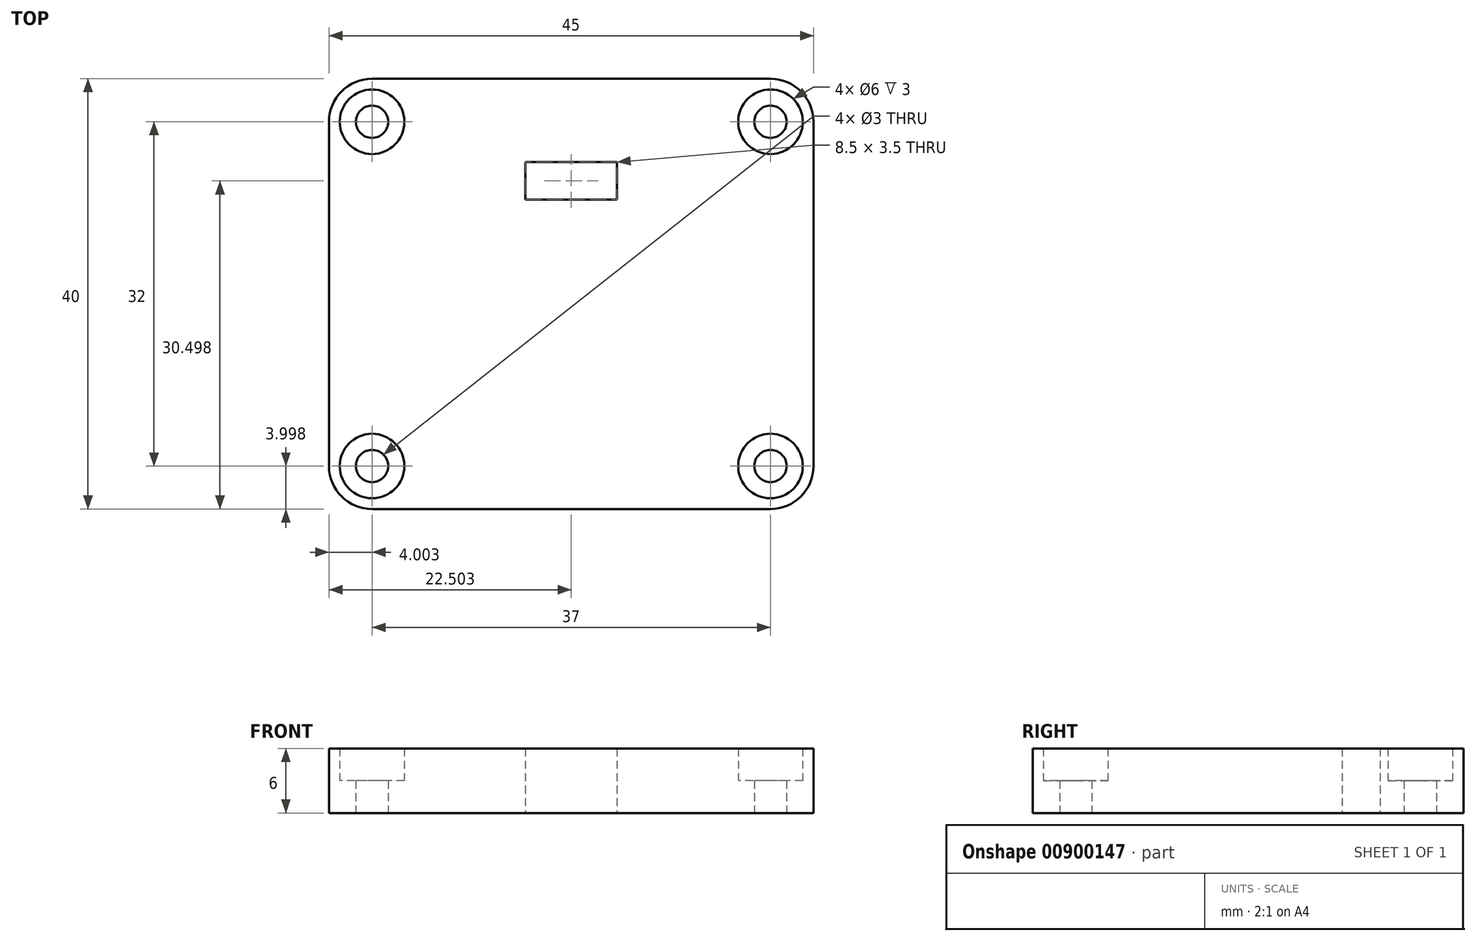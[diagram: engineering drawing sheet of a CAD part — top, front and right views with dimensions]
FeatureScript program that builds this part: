
annotation { "Feature Type Name" : "Feature", "Feature Type Description" : "" }
export const myFeature = defineFeature(function(context is Context, id is Id, definition is map)
    precondition{}
    {
        {
            var Q0;
            Q0=qCreatedBy(makeId("Top.planeOp"),FACE);
            var sketch = newSketch(context, id + "F0", { "sketchPlane" : qUnion([Q0])});
            skLineSegment(sketch, "E0", {"start": v(-24.6, 14.45) * mm, "end": v(-24.6, -17.55) * mm});
            skLineSegment(sketch, "E1", {"start": v(-20.6, -21.55) * mm, "end": v(16.4, -21.55) * mm});
            skLineSegment(sketch, "E2", {"start": v(20.4, -17.55) * mm, "end": v(20.4, 14.45) * mm});
            skLineSegment(sketch, "E3", {"start": v(16.4, 18.45) * mm, "end": v(-20.6, 18.45) * mm});
            skPoint(sketch, "E4.visualSharp", {"position": v(-24.6, 18.45) * mm});
            skArc(sketch, "E4.filletArc", {"start": v(-20.6, 18.45) * mm, "mid": v(-23.44, 17.28) * mm, "end": v(-24.6, 14.45) * mm});
            skPoint(sketch, "E5.visualSharp", {"position": v(20.4, 18.45) * mm});
            skArc(sketch, "E5.filletArc", {"start": v(20.4, 14.45) * mm, "mid": v(19.22, 17.28) * mm, "end": v(16.4, 18.45) * mm});
            skPoint(sketch, "E6.visualSharp", {"position": v(20.4, -21.55) * mm});
            skArc(sketch, "E6.filletArc", {"start": v(16.4, -21.55) * mm, "mid": v(19.22, -20.38) * mm, "end": v(20.4, -17.55) * mm});
            skPoint(sketch, "E7.visualSharp", {"position": v(-24.6, -21.55) * mm});
            skArc(sketch, "E7.filletArc", {"start": v(-24.6, -17.55) * mm, "mid": v(-23.44, -20.38) * mm, "end": v(-20.6, -21.55) * mm});
            skCircle(sketch, "E8", {"center": v(-20.6, 14.45) * mm, "radius": 1.5 * mm});
            skCircle(sketch, "E9", {"center": v(16.4, 14.45) * mm, "radius": 1.5 * mm});
            skCircle(sketch, "E10", {"center": v(16.4, -17.55) * mm, "radius": 1.5 * mm});
            skCircle(sketch, "E11", {"center": v(-20.6, -17.55) * mm, "radius": 1.5 * mm});
            skLineSegment(sketch, "E12", {"start": v(-14.36, 10.7) * mm, "end": v(-14.36, -13.8) * mm});
            skLineSegment(sketch, "E13", {"start": v(-14.36, -13.8) * mm, "end": v(10.14, -13.8) * mm});
            skLineSegment(sketch, "E14", {"start": v(10.14, -13.8) * mm, "end": v(10.14, 10.7) * mm});
            skLineSegment(sketch, "E15", {"start": v(10.14, 10.7) * mm, "end": v(-14.36, 10.7) * mm});
            skLineSegment(sketch, "E16", {"start": v(-6.36, 7.2) * mm, "end": v(2.14, 7.2) * mm});
            skLineSegment(sketch, "E17", {"start": v(2.14, 7.2) * mm, "end": v(2.14, 10.7) * mm});
            skLineSegment(sketch, "E18", {"start": v(-6.36, 7.2) * mm, "end": v(-6.36, 10.7) * mm});
            skLineSegment(sketch, "E19", {"start": v(-2.1, 18.45) * mm, "end": v(-2.1, -21.55) * mm, "construction": true});
            skLineSegment(sketch, "E20", {"start": v(-24.6, -1.55) * mm, "end": v(20.4, -1.55) * mm, "construction": true});
            skCircle(sketch, "E21", {"center": v(-20.6, 14.45) * mm, "radius": 3 * mm});
            skCircle(sketch, "E22.MirrorC", {"center": v(16.4, 14.45) * mm, "radius": 3 * mm});
            skCircle(sketch, "E23.MirrorC", {"center": v(16.4, -17.55) * mm, "radius": 3 * mm});
            skCircle(sketch, "E24.MirrorC", {"center": v(-20.6, -17.55) * mm, "radius": 3 * mm});
            skSolve(sketch);
        }
        {
            var Q0;
            Q0 = qSketchRegion(id + "F0", true);
            var Q1;
            {var subQ3=sQuery(id+"F0.wireOp",EDGE,"E12");Q1=makeQuery(id+"F0.imprint","IMPRINT",FACE,{"disambiguationData":[TD([[makeQuery(id+"F0.imprint","IMPRINT",EDGE,{"derivedFrom":subQ3}),1.0]])]});}
            extrude(context, id + "F1", {"entities" : qUnion([Q0, Q1]), "depth" : 6 * mm, "offsetDistance" : 25 * mm});
        }
        {
            var Q0;
            Q0=makeQuery(id+"F0.imprint","IMPRINT",FACE,{"disambiguationData":[TD([[makeQuery(id+"F0.imprint","IMPRINT",EDGE,{"derivedFrom":sQuery(id+"F0.wireOp",EDGE,"E8")}),-1.0]])]});
            var Q1;
            Q1=makeQuery(id+"F0.imprint","IMPRINT",FACE,{"disambiguationData":[TD([[makeQuery(id+"F0.imprint","IMPRINT",EDGE,{"derivedFrom":sQuery(id+"F0.wireOp",EDGE,"E9")}),-1.0]])]});
            var Q2;
            Q2=makeQuery(id+"F0.imprint","IMPRINT",FACE,{"disambiguationData":[TD([[makeQuery(id+"F0.imprint","IMPRINT",EDGE,{"derivedFrom":sQuery(id+"F0.wireOp",EDGE,"E10")}),-1.0]])]});
            var Q3;
            Q3=makeQuery(id+"F0.imprint","IMPRINT",FACE,{"disambiguationData":[TD([[makeQuery(id+"F0.imprint","IMPRINT",EDGE,{"derivedFrom":sQuery(id+"F0.wireOp",EDGE,"E11")}),-1.0]])]});
            extrude(context, id + "F2", {"entities" : qUnion([Q0, Q1, Q2, Q3]), "operationType" : NewBodyOperationType.ADD, "depth" : 3 * mm, "offsetDistance" : 25 * mm});
        }
    });
